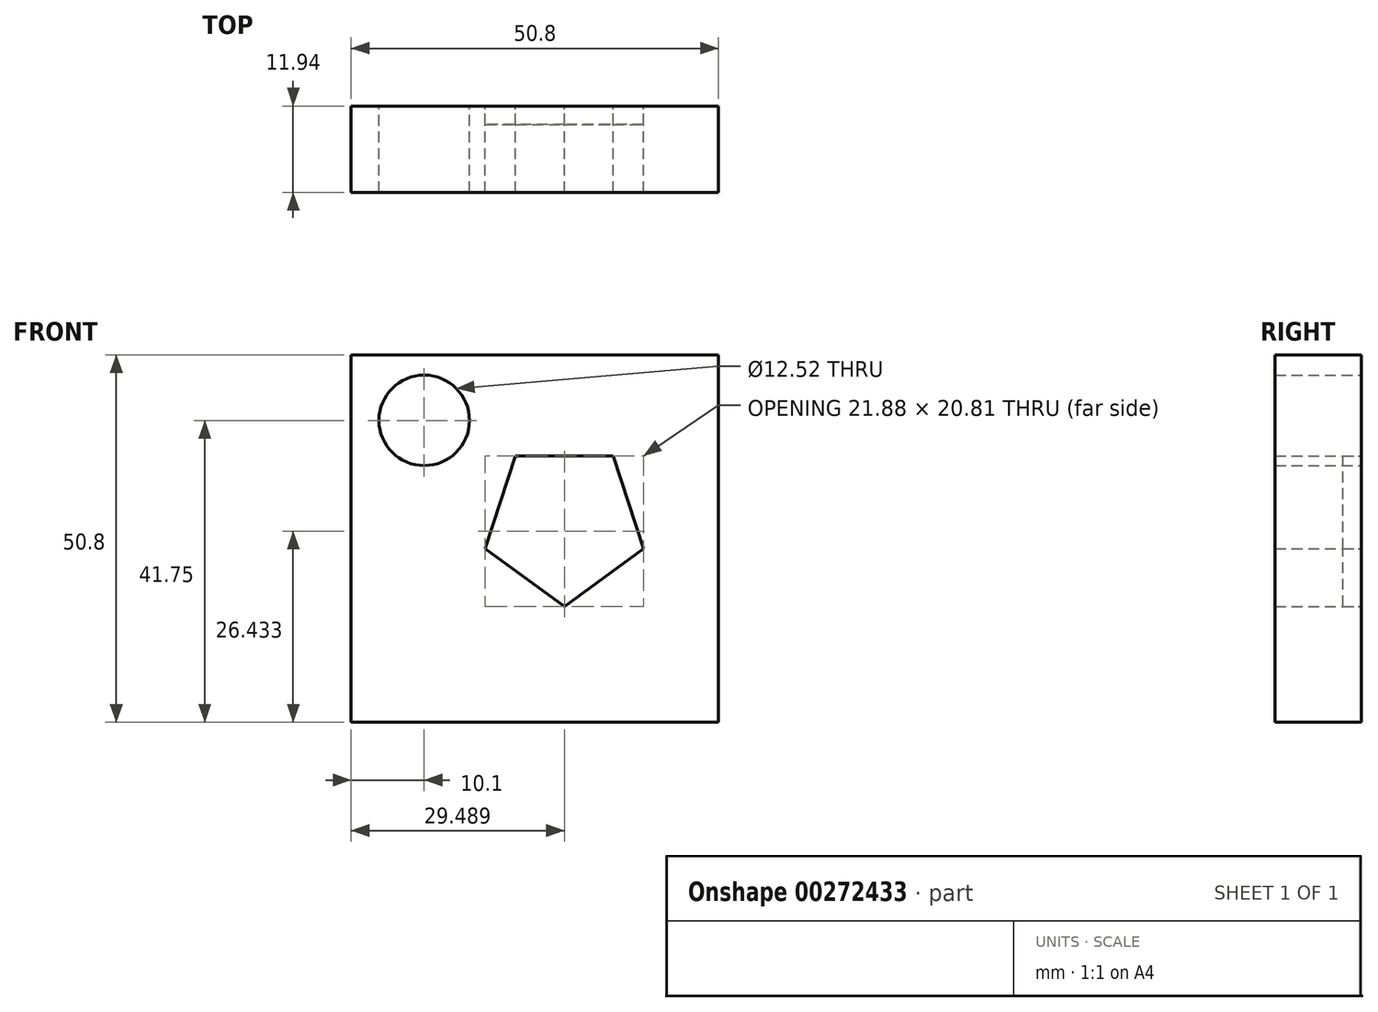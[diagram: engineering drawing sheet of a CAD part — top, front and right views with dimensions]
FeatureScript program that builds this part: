
annotation { "Feature Type Name" : "Feature", "Feature Type Description" : "" }
export const myFeature = defineFeature(function(context is Context, id is Id, definition is map)
    precondition{}
    {
        {
            var Q0;
            Q0=qCreatedBy(makeId("Front.planeOp"),FACE);
            var sketch = newSketch(context, id + "F0", { "sketchPlane" : qUnion([Q0])});
            skLineSegment(sketch, "E0.bottom", {"start": v(-100.58, 50.8) * mm, "end": v(-49.78, 50.8) * mm});
            skLineSegment(sketch, "E0.top", {"start": v(-100.58, 0) * mm, "end": v(-49.78, 0) * mm});
            skLineSegment(sketch, "E0.left", {"start": v(-100.58, 50.8) * mm, "end": v(-100.58, 0) * mm});
            skLineSegment(sketch, "E0.right", {"start": v(-49.78, 50.8) * mm, "end": v(-49.78, 0) * mm});
            skCircle(sketch, "E1", {"center": v(-90.48, 41.75) * mm, "radius": 6.26 * mm});
            skCircle(sketch, "E2.cCircle", {"center": v(-71.1, 27.53) * mm, "radius": 9.3 * mm, "construction": true});
            skLineSegment(sketch, "E2.0", {"start": v(-77.85, 36.84) * mm, "end": v(-64.33, 36.84) * mm});
            skLineSegment(sketch, "E2.1", {"start": v(-64.33, 36.84) * mm, "end": v(-60.15, 23.98) * mm});
            skLineSegment(sketch, "E2.2", {"start": v(-60.15, 23.98) * mm, "end": v(-71.1, 16.03) * mm});
            skLineSegment(sketch, "E2.3", {"start": v(-71.1, 16.03) * mm, "end": v(-82.03, 23.98) * mm});
            skLineSegment(sketch, "E2.4", {"start": v(-82.03, 23.98) * mm, "end": v(-77.85, 36.84) * mm});
            skPoint(sketch, "E2.0.midPoint", {"position": v(-71.1, 36.84) * mm});
            skSolve(sketch);
        }
        {
            var Q0;
            Q0=makeQuery(id+"F0.imprint","IMPRINT",FACE,{"disambiguationData":[TD([[makeQuery(id+"F0.imprint","IMPRINT",EDGE,{"derivedFrom":sQuery(id+"F0.wireOp",EDGE,"E2.0")}),-1.0]])]});
            extrude(context, id + "F1", {"entities" : qUnion([Q0]), "depth" : 2.54 * mm});
        }
        {
            var Q0;
            Q0 = qSketchRegion(id + "F0", true);
            extrude(context, id + "F2", {"entities" : qUnion([Q0]), "depth" : 11.94 * mm});
        }
    });
